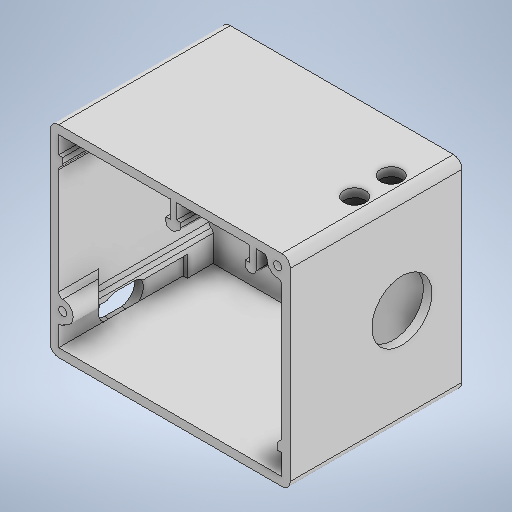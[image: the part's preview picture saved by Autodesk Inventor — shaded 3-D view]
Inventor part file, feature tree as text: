
AUTODESK INVENTOR PART (.ipt)
format: ipt  version: 2025.2 (Build 292293000, 293)  size: 564,224 bytes
history: native  units: mm
features: extrude x14, sketch x14, projected_geometry x12, fillet x3, chamfer x2
ambient origin geometry x8: Origin, YZ Plane, XZ Plane, XY Plane, X Axis, Y Axis, Z Axis, Center Point
bodies: Volumenkörper1 (feature_tree)
feature tree (45):
  extrude  "Extrusion1"  Depth=47.0mm
  extrude  "Extrusion2"  Depth=2.0mm
  extrude  "Extrusion3"  Depth=35.0mm TaperAngle=0.0deg
  extrude  "Extrusion4"  Depth=2.0mm
  extrude  "Extrusion5"  Depth=2.0mm
  extrude  "Extrusion6"  Depth=4.1mm
  extrude  "Extrusion10"  Depth=1.0mm
  extrude  "Extrusion11"  Depth=26.0mm
  extrude  "Extrusion12"  Depth=2.0mm
  extrude  "Extrusion14"  Depth=2.0mm
  extrude  "Extrusion15"  Depth=2.5mm
  extrude  "Extrusion16"  Depth=30.0mm TaperAngle=0.0deg
  chamfer  "Fasen1"  Distance=3.0mm
  chamfer  "Fasen2"  Distance=8.5mm
  extrude  "Extrusion17"  Depth=4.0mm
  fillet  "Rundung1"  Radius=10.0mm
  fillet  "Rundung2"  Radius=14.0mm
  fillet  "Rundung3"  Radius=6.0mm
  extrude  "Extrusion18"  Depth=4.0mm
  sketch  "Skizze1"  dims[d0=56.0mm d1=47.0mm]
  sketch  "Skizze2"  dims[d2=2.0mm d3=0.0mm d4=2.0mm]
  projected_geometry  "Projizierte Kontur1"
  sketch  "Skizze3"  dims[d5=2.0mm d6=35.0mm d7=0.0mm]
  projected_geometry  "Projizierte Kontur2"
  projected_geometry  "Projizierte Kontur3"
  sketch  "Skizze4"  dims[d8=4.85mm d9=2.0mm]
  sketch  "Skizze5"  dims[d10=1.0mm d11=2.0mm]
  projected_geometry  "Projizierte Kontur4"
  sketch  "Skizze6"  dims[d12=1.0mm d13=4.1mm]
  projected_geometry  "Projizierte Kontur5"
  projected_geometry  "Projizierte Kontur6"
  sketch  "Skizze10"  dims[d14=2.0mm d15=1.0mm]
  projected_geometry  "Projizierte Kontur10"
  sketch  "Skizze11"  dims[d16=26.0mm d17=3.5mm]
  projected_geometry  "Projizierte Kontur11"
  sketch  "Skizze12"  dims[d18=1.5mm d19=2.0mm]
  projected_geometry  "Projizierte Kontur12"
  sketch  "Skizze15"  dims[d20=1.0mm d21=2.0mm]
  projected_geometry  "Projizierte Kontur14"
  sketch  "Skizze16"  dims[d22=1.5mm d23=2.5mm]
  sketch  "Skizze17"  dims[d24=17.0mm d25=30.0mm d26=0.0mm]
  projected_geometry  "Projizierte Kontur15"
  sketch  "Skizze18"  dims[d27=5.0mm]
  sketch  "Skizze19"  dims[d28=5.0mm d29=3.0mm d30=8.5mm d31=8.5mm d32=10.0mm d33=0.0mm d34=14.0mm d35=0.0mm d36=6.0mm d37=0.0mm d48=14.0mm d49=9.0mm d50=4.75mm d51=0.0mm d52=10.5mm d53=6.5mm d54=2.0mm d55=0.0mm d56=2.0mm d57=0.0mm d60=3.0mm d61=0.0mm d62=3.2mm d63=20.2mm d64=135.0deg d65=135.0deg d66=30.0mm d67=0.0mm d68=1.9mm d69=1.9mm d70=1.5mm d71=1.5mm d72=6.0mm d73=0.0mm d74=3.35mm d75=2.0mm d76=45.0deg d77=3.35mm d78=2.0mm d79=45.0deg d80=1.9mm d81=1.9mm d82=6.5mm d83=0.0mm d84=1.0mm d85=0.5mm d86=2.0mm d87=4.0mm d88=0.0mm]
  projected_geometry  "Projizierte Kontur16"
